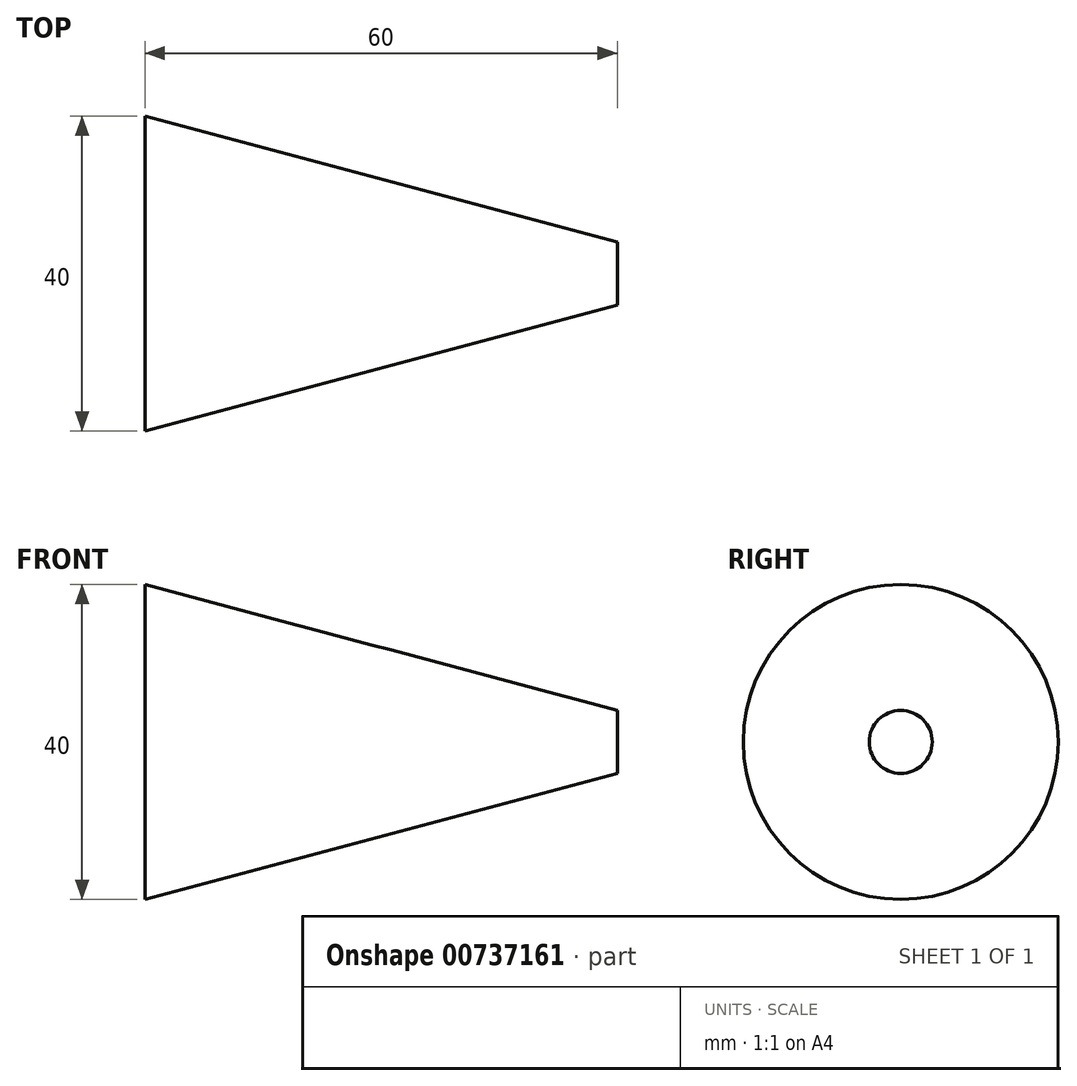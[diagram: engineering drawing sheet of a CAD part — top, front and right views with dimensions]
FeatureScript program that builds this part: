
annotation { "Feature Type Name" : "Feature", "Feature Type Description" : "" }
export const myFeature = defineFeature(function(context is Context, id is Id, definition is map)
    precondition{}
    {
        {
            var Q0;
            Q0=qCreatedBy(makeId("Front.planeOp"),FACE);
            var sketch = newSketch(context, id + "F0", { "sketchPlane" : qUnion([Q0])});
            skLineSegment(sketch, "E0", {"start": v(-68.19, 24.3) * mm, "end": v(-8.19, 24.3) * mm});
            skLineSegment(sketch, "E1", {"start": v(-68.19, 24.3) * mm, "end": v(-68.19, 44.3) * mm});
            skLineSegment(sketch, "E2", {"start": v(-68.19, 44.3) * mm, "end": v(-8.19, 28.3) * mm});
            skLineSegment(sketch, "E3", {"start": v(-8.19, 28.3) * mm, "end": v(-8.19, 24.3) * mm});
            skLineSegment(sketch, "E4", {"start": v(-112.03, 24.3) * mm, "end": v(40.53, 24.3) * mm});
            skSolve(sketch);
        }
        {
            var Q0;
            {var subQ0=sQuery(id+"F0.wireOp",EDGE,"E1");Q0=makeQuery(id+"F0.imprint","IMPRINT",FACE,{"disambiguationData":[TD([[makeQuery(id+"F0.imprint","IMPRINT",EDGE,{"derivedFrom":subQ0}),-1.0]])]});}
            var Q1;
            Q1=sQuery(id+"F0.wireOp",EDGE,"E4");
            revolve(context, id + "F1", {"surfaceOperationType" : NewSurfaceOperationType.NEW, "entities" : qUnion([Q0]), "axis" : qUnion([Q1]), "revolveType" : RevolveType.FULL});
        }
    });
